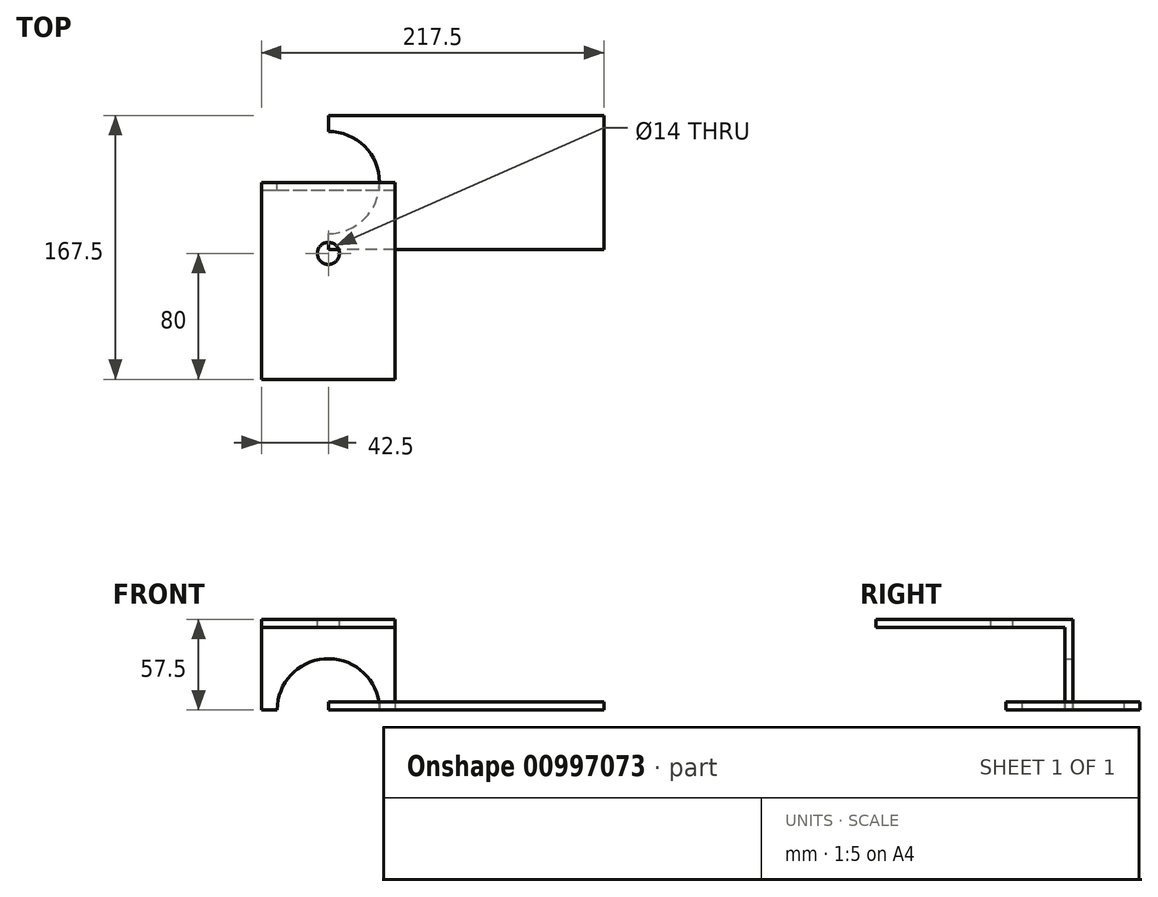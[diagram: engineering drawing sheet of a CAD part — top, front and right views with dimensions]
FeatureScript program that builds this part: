
annotation { "Feature Type Name" : "Feature", "Feature Type Description" : "" }
export const myFeature = defineFeature(function(context is Context, id is Id, definition is map)
    precondition{}
    {
        {
            var Q0;
            Q0=qCreatedBy(makeId("Front.planeOp"),FACE);
            var sketch = newSketch(context, id + "F0", { "sketchPlane" : qUnion([Q0])});
            skArc(sketch, "E0", {"start": v(32.5, 0) * mm, "mid": v(0, 32.5) * mm, "end": v(-32.5, 0) * mm});
            skLineSegment(sketch, "E1", {"start": v(-32.5, 0) * mm, "end": v(-42.5, 0) * mm});
            skLineSegment(sketch, "E2", {"start": v(-42.5, 0) * mm, "end": v(-42.5, 57.5) * mm});
            skLineSegment(sketch, "E3", {"start": v(-42.5, 57.5) * mm, "end": v(42.5, 57.5) * mm});
            skLineSegment(sketch, "E4", {"start": v(42.5, 57.5) * mm, "end": v(42.5, 0) * mm});
            skLineSegment(sketch, "E5", {"start": v(42.5, 0) * mm, "end": v(32.5, 0) * mm});
            skSolve(sketch);
        }
        {
            var Q0;
            Q0 = qSketchRegion(id + "F0", true);
            extrude(context, id + "F1", {"entities" : qUnion([Q0]), "depth" : 5 * mm, "offsetDistance" : 25 * mm});
        }
        {
            var Q0;
            Q0=makeQuery(id+"F1.opExtrude","SWEPT_FACE",FACE,{"disambiguationData":[OSD([sQuery(id+"F0.wireOp",EDGE,"E3")])]});
            var sketch = newSketch(context, id + "F2", { "sketchPlane" : qUnion([Q0])});
            skPoint(sketch, "E6.oppositeSnap0", {"position": v(42.5, -2.5) * mm});
            skLineSegment(sketch, "E6.bottom", {"start": v(-42.5, 0) * mm, "end": v(42.5, 0) * mm});
            skLineSegment(sketch, "E6.top", {"start": v(-42.5, -125) * mm, "end": v(42.5, -125) * mm});
            skLineSegment(sketch, "E6.left", {"start": v(-42.5, 0) * mm, "end": v(-42.5, -125) * mm});
            skLineSegment(sketch, "E6.right", {"start": v(42.5, 0) * mm, "end": v(42.5, -125) * mm});
            skCircle(sketch, "E7", {"center": v(0, -45) * mm, "radius": 7 * mm});
            skSolve(sketch);
        }
        {
            var Q0;
            Q0 = qSketchRegion(id + "F2", true);
            extrude(context, id + "F3", {"entities" : qUnion([Q0]), "operationType" : NewBodyOperationType.ADD, "oppositeDirection" : true, "depth" : 5 * mm, "offsetDistance" : 25 * mm});
        }
        {
            var Q0;
            Q0=qCreatedBy(makeId("Top.planeOp"),FACE);
            var sketch = newSketch(context, id + "F4", { "sketchPlane" : qUnion([Q0])});
            skArc(sketch, "E8", {"start": v(0, -32.5) * mm, "mid": v(32.5, 0) * mm, "end": v(0, 32.5) * mm});
            skLineSegment(sketch, "E9", {"start": v(0, 32.5) * mm, "end": v(0, 42.5) * mm});
            skLineSegment(sketch, "E10", {"start": v(0, 42.5) * mm, "end": v(175, 42.5) * mm});
            skLineSegment(sketch, "E11", {"start": v(175, 42.5) * mm, "end": v(175, -42.5) * mm});
            skLineSegment(sketch, "E12", {"start": v(175, -42.5) * mm, "end": v(0, -42.5) * mm});
            skLineSegment(sketch, "E13", {"start": v(0, -42.5) * mm, "end": v(0, -32.5) * mm});
            skSolve(sketch);
        }
        {
            var Q0;
            Q0=makeQuery(id+"F4.imprint","IMPRINT",FACE,{"disambiguationData":[TD([[makeQuery(id+"F4.imprint","IMPRINT",EDGE,{"derivedFrom":sQuery(id+"F4.wireOp",EDGE,"E8")}),-1.0]])]});
            extrude(context, id + "F5", {"entities" : qUnion([Q0]), "depth" : 5 * mm, "offsetDistance" : 25 * mm});
        }
    });
